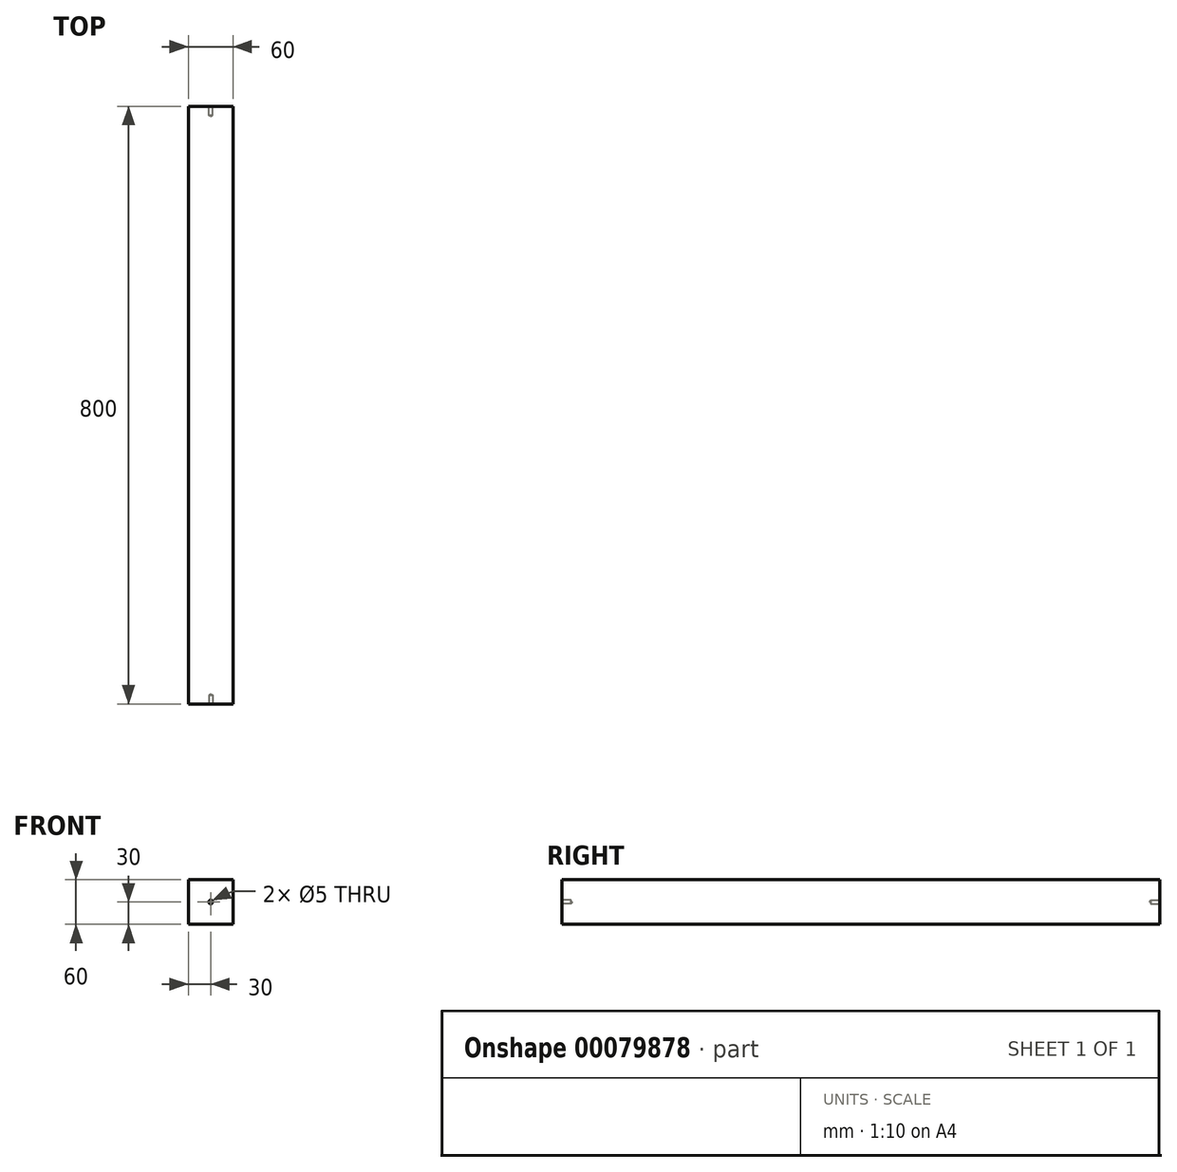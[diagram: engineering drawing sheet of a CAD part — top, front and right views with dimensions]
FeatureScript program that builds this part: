
annotation { "Feature Type Name" : "Feature", "Feature Type Description" : "" }
export const myFeature = defineFeature(function(context is Context, id is Id, definition is map)
    precondition{}
    {
        {
            assignVariable(context, id + "F0", {"name" : "bed_width", "anyValue" : 800});
        }
        {
            assignVariable(context, id + "F1", {"name" : "hole_length", "anyValue" : 12});
        }
        {
            assignVariable(context, id + "F2", {"name" : "hole_diameter", "anyValue" : 5});
        }
        {
            var Q0;
            Q0=qCreatedBy(makeId("Front.planeOp"),FACE);
            var sketch = newSketch(context, id + "F3", { "sketchPlane" : qUnion([Q0])});
            skLineSegment(sketch, "E0.bottom", {"start": v(0, 0) * mm, "end": v(60, 0) * mm});
            skLineSegment(sketch, "E0.top", {"start": v(0, 60) * mm, "end": v(60, 60) * mm});
            skLineSegment(sketch, "E0.left", {"start": v(0, 0) * mm, "end": v(0, 60) * mm});
            skLineSegment(sketch, "E0.right", {"start": v(60, 0) * mm, "end": v(60, 60) * mm});
            skSolve(sketch);
        }
        {
            var Q0;
            Q0=makeQuery(id+"F3.imprint","IMPRINT",FACE,{"disambiguationData":[TD([[makeQuery(id+"F3.imprint","IMPRINT",EDGE,{"derivedFrom":sQuery(id+"F3.wireOp",EDGE,"E0.bottom")}),1.0]])]});
            extrude(context, id + "F4", {"entities" : qUnion([Q0]), "depth" : (getVariable(context, 'bed_width')) * mm});
        }
        {
            var Q0;
            Q0=makeQuery(id+"F4.opExtrude","CAP_FACE",FACE,{"disambiguationData":[OSD([sQuery(id+"F3.wireOp",EDGE,"E0.bottom"),sQuery(id+"F3.wireOp",EDGE,"E0.top"),sQuery(id+"F3.wireOp",EDGE,"E0.left"),sQuery(id+"F3.wireOp",EDGE,"E0.right")])],"isStart":true});
            var sketch = newSketch(context, id + "F5", { "sketchPlane" : qUnion([Q0])});
            skPoint(sketch, "E1", {"position": v(-30, 30) * mm});
            skPoint(sketch, "E1.positionSnap0", {"position": v(-30, 0) * mm});
            skPoint(sketch, "E1.positionSnap1", {"position": v(-60, 30) * mm});
            skSolve(sketch);
        }
        {
            var Q0;
            Q0=makeQuery(id+"F4.opExtrude","CAP_FACE",FACE,{"disambiguationData":[OSD([sQuery(id+"F3.wireOp",EDGE,"E0.bottom"),sQuery(id+"F3.wireOp",EDGE,"E0.top"),sQuery(id+"F3.wireOp",EDGE,"E0.left"),sQuery(id+"F3.wireOp",EDGE,"E0.right")])],"isStart":false});
            var sketch = newSketch(context, id + "F6", { "sketchPlane" : qUnion([Q0])});
            skPoint(sketch, "E2", {"position": v(30, 30) * mm});
            skPoint(sketch, "E2.positionSnap0", {"position": v(60, 30) * mm});
            skPoint(sketch, "E2.positionSnap1", {"position": v(30, 0) * mm});
            skSolve(sketch);
        }
        {
            var Q0;
            Q0=sQuery(id+"F6.wireOp",VERTEX,"E2");
            var Q1;
            Q1=sQuery(id+"F5.wireOp",VERTEX,"E1");
            var Q2;
            Q2=makeQuery(id+"F4.opExtrude","SWEPT_BODY",BODY,{"disambiguationData":[OSD([sQuery(id+"F3.wireOp",EDGE,"E0.bottom"),sQuery(id+"F3.wireOp",EDGE,"E0.top"),sQuery(id+"F3.wireOp",EDGE,"E0.left"),sQuery(id+"F3.wireOp",EDGE,"E0.right")])]});
            hole(context, id + "F7", {"style" : HoleStyle.SIMPLE, "endStyle" : HoleEndStyle.BLIND, "holeDiameter" : (getVariable(context, 'hole_diameter')) * mm, "holeDepth" : (getVariable(context, 'hole_length')) * mm, "startFromSketch" : true, "locations" : qUnion([Q0, Q1]), "scope" : qUnion([Q2])});
        }
    });
